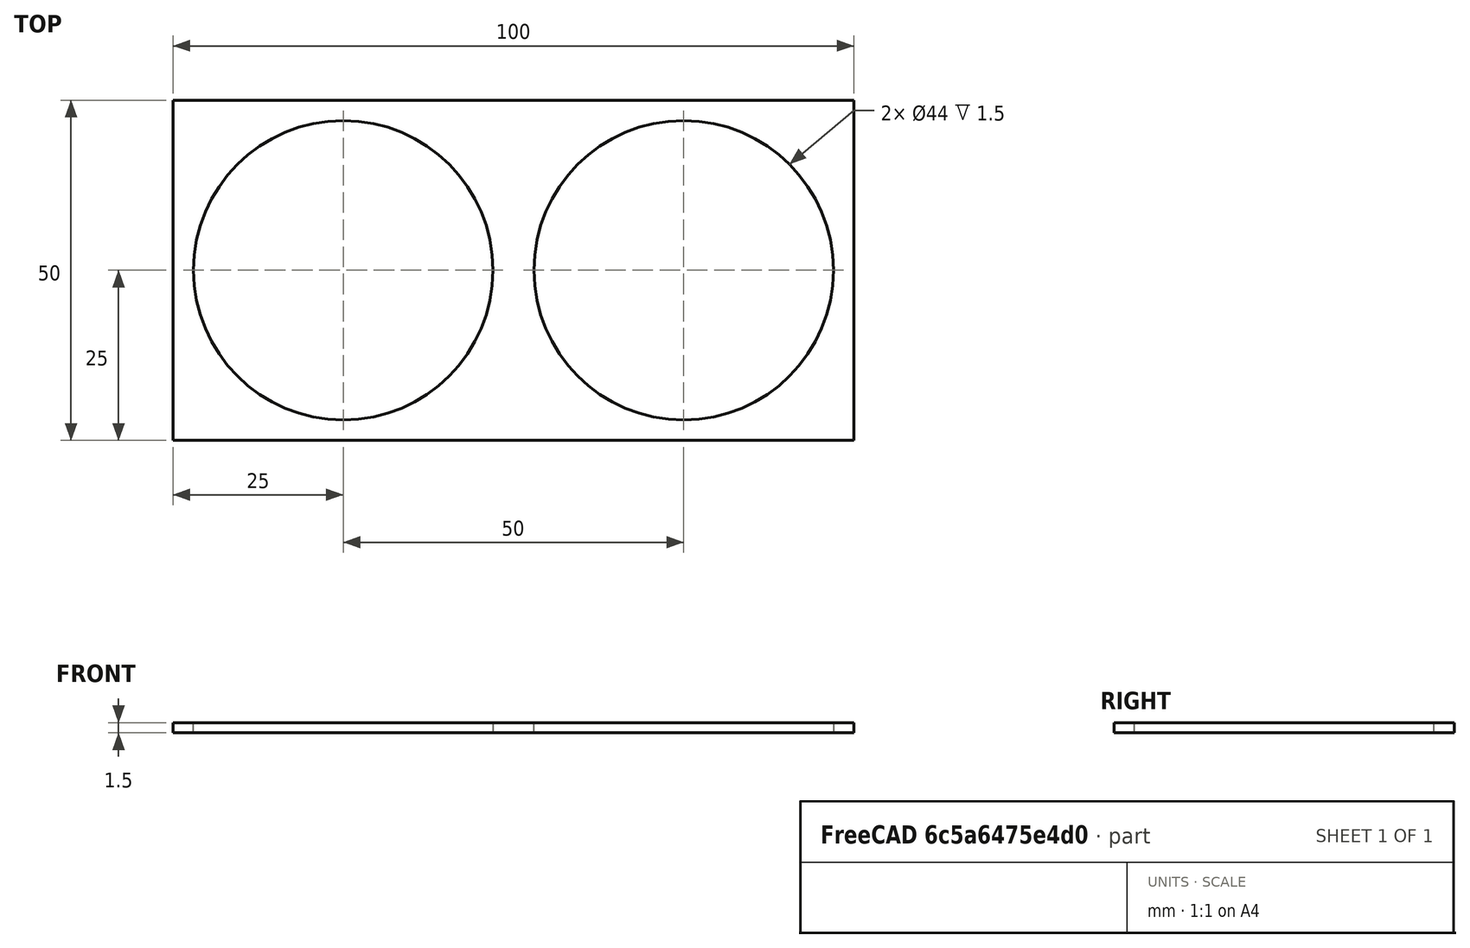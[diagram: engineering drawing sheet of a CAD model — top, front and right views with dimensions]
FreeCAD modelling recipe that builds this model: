
FCSTD DOCUMENT  (FreeCAD 0.19R24276 (Git))
Label: piezo_holder_gasket_mold_A_v0.5
License: All rights reserved
LicenseURL: http://en.wikipedia.org/wiki/All_rights_reserved
objects: Sketcher::SketchObject×1, PartDesign::Pad×1, PartDesign::Body×1, App::Part×1
note: 4 computed .brp shape members not serialized (recipe doc carries the construction recipe); baked Part::Feature solids carry a one-line shape summary decoded from their .brp

FEATURE [Sketcher::SketchObject] Sketch001
  FullyConstrained = true
  MapMode = 5
  Placement = pos=(0,0,0) rot=(1,0,0;3.14159rad)
  sketch-geometry (6):
    g0: Circle CenterX=0 CenterY=0 CenterZ=0 NormalX=0 NormalY=0 NormalZ=1 AngleXU=0 Radius=22
    g1: LineSegment StartX=-25 StartY=25 StartZ=0 EndX=75 EndY=25 EndZ=0
    g2: LineSegment StartX=75 StartY=25 StartZ=0 EndX=75 EndY=-25 EndZ=0
    g3: LineSegment StartX=75 StartY=-25 StartZ=0 EndX=-25 EndY=-25 EndZ=0
    g4: LineSegment StartX=-25 StartY=-25 StartZ=0 EndX=-25 EndY=25 EndZ=0
    g5: Circle CenterX=50 CenterY=0 CenterZ=0 NormalX=0 NormalY=0 NormalZ=1 AngleXU=0 Radius=22
  constraints (16):
    c: Coincident(g0,g-1)
    c: Radius(g0) = 22
    c: Coincident(g1,g2)
    c: Coincident(g2,g3)
    c: Coincident(g3,g4)
    c: Coincident(g4,g1)
    c: Horizontal(g3)
    c: Vertical(g2)
    c: Symmetric(g1,g3,g-1)
    c: DistanceY(g4,g4) = 50
    c: DistanceX(g1,g0) = 25
    c: PointOnObject(g5,g-1)
    c: Equal(g5,g0)
    c: DistanceX(g0,g5) = 50
    c: DistanceX(g5,g1) = 25
    c: Equal(g2,g4)
FEATURE [PartDesign::Pad] Pad
  Direction = (1,1,1)
  Length = 1.5
  Length2 = 100
  Placement = pos=(0,0,0) rot=(1,0,0;3.14159rad)
  Profile = -> Sketch001
  Type = 0
FEATURE [PartDesign::Body] Fillet002Body
  Group = -> [Sketch001,Pad]
  Origin = -> Origin001
  Tip = -> Pad
FEATURE [App::Part] Part
  Group = -> [Fillet002Body]
  Origin = -> Origin
